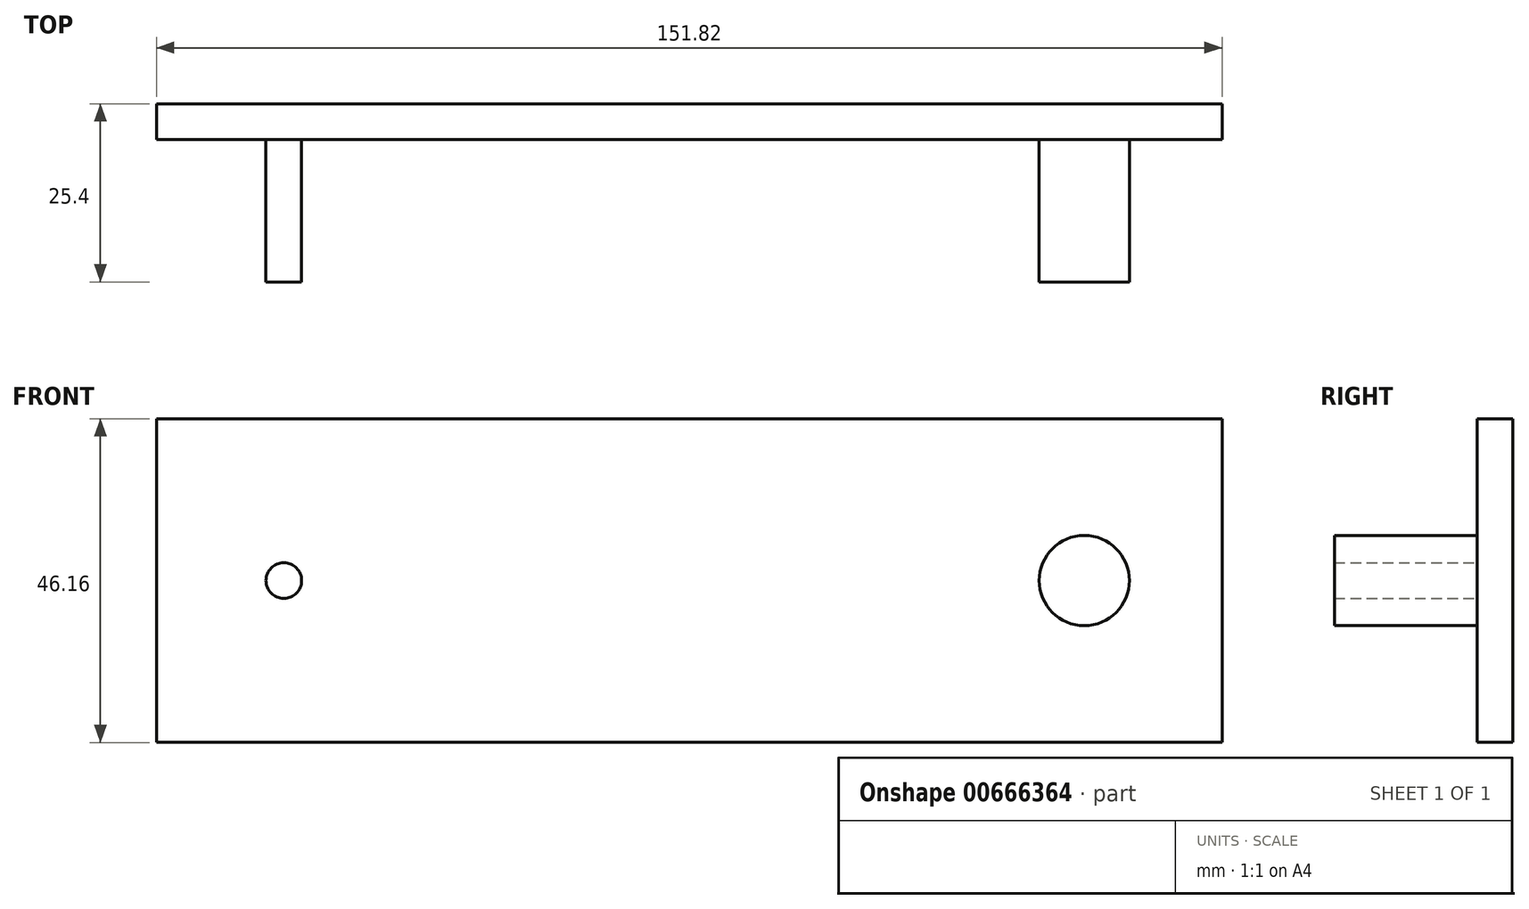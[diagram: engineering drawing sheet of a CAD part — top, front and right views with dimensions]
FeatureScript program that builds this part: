
annotation { "Feature Type Name" : "Feature", "Feature Type Description" : "" }
export const myFeature = defineFeature(function(context is Context, id is Id, definition is map)
    precondition{}
    {
        {
            var Q0;
            Q0=qCreatedBy(makeId("Front.planeOp"),FACE);
            var sketch = newSketch(context, id + "F0", { "sketchPlane" : qUnion([Q0])});
            skLineSegment(sketch, "E0.bottom", {"start": v(75.91, 23.08) * mm, "end": v(-75.91, 23.08) * mm});
            skLineSegment(sketch, "E0.top", {"start": v(75.91, -23.08) * mm, "end": v(-75.91, -23.08) * mm});
            skLineSegment(sketch, "E0.left", {"start": v(75.91, 23.08) * mm, "end": v(75.91, -23.08) * mm});
            skLineSegment(sketch, "E0.right", {"start": v(-75.91, 23.08) * mm, "end": v(-75.91, -23.08) * mm});
            skPoint(sketch, "E0.middle", {"position": v(0, 0) * mm});
            skCircle(sketch, "E1", {"center": v(-57.77, 0) * mm, "radius": 2.54 * mm});
            skCircle(sketch, "E2", {"center": v(56.28, 0) * mm, "radius": 6.42 * mm});
            skSolve(sketch);
        }
        {
            var Q0;
            Q0=makeQuery(id+"F0.imprint","IMPRINT",FACE,{"disambiguationData":[TD([[makeQuery(id+"F0.imprint","IMPRINT",EDGE,{"derivedFrom":sQuery(id+"F0.wireOp",EDGE,"E0.bottom")}),1.0]])]});
            extrude(context, id + "F1", {"entities" : qUnion([Q0]), "depth" : 5.08 * mm, "offsetDistance" : 25.4 * mm});
        }
        {
            var Q0;
            Q0=makeQuery(id+"F0.imprint","IMPRINT",FACE,{"disambiguationData":[TD([[makeQuery(id+"F0.imprint","IMPRINT",EDGE,{"derivedFrom":sQuery(id+"F0.wireOp",EDGE,"E1")}),1.0]])]});
            var Q1;
            Q1=makeQuery(id+"F0.imprint","IMPRINT",FACE,{"disambiguationData":[TD([[makeQuery(id+"F0.imprint","IMPRINT",EDGE,{"derivedFrom":sQuery(id+"F0.wireOp",EDGE,"E2")}),1.0]])]});
            extrude(context, id + "F2", {"entities" : qUnion([Q0, Q1]), "operationType" : NewBodyOperationType.ADD, "depth" : 25.4 * mm, "offsetDistance" : 25.4 * mm});
        }
    });
